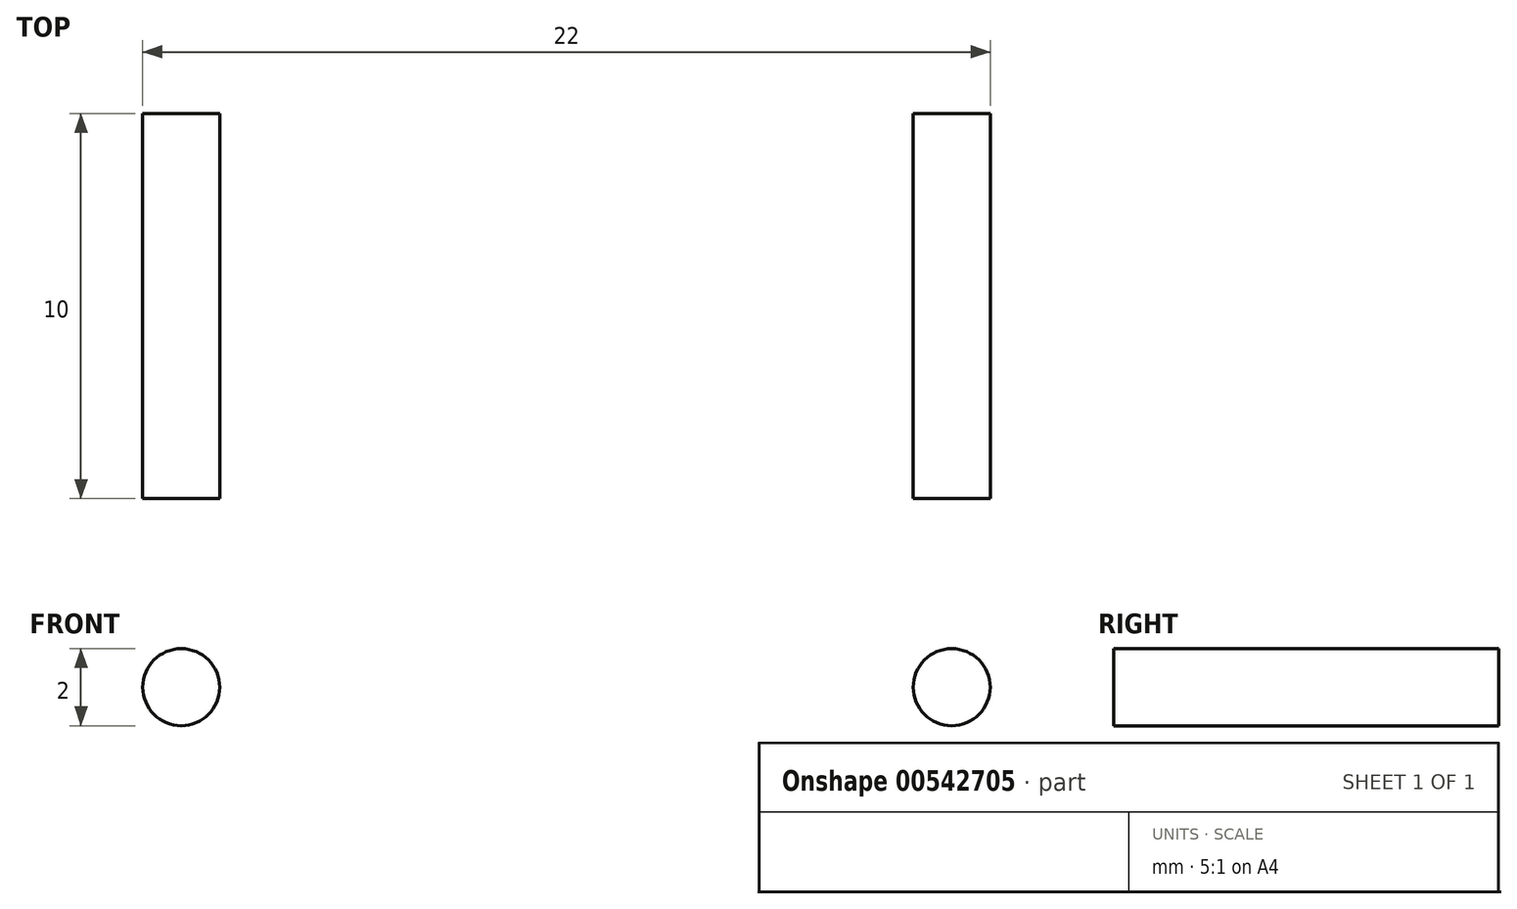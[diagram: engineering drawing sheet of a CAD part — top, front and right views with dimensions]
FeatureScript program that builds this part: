
annotation { "Feature Type Name" : "Feature", "Feature Type Description" : "" }
export const myFeature = defineFeature(function(context is Context, id is Id, definition is map)
    precondition{}
    {
        {
            var Q0;
            Q0=qCreatedBy(makeId("Front.planeOp"),FACE);
            var sketch = newSketch(context, id + "F0", { "sketchPlane" : qUnion([Q0])});
            skArc(sketch, "E0", {"start": v(-9.06, -4.23) * mm, "mid": v(0, 10) * mm, "end": v(9.06, -4.23) * mm});
            skLineSegment(sketch, "E1", {"start": v(-9.06, -4.23) * mm, "end": v(0, 0) * mm, "construction": true});
            skLineSegment(sketch, "E2", {"start": v(9.06, -4.23) * mm, "end": v(0, 0) * mm, "construction": true});
            skLineSegment(sketch, "E3", {"start": v(-9.75, 10.9) * mm, "end": v(-9.75, -4.03) * mm, "construction": true});
            skLineSegment(sketch, "E4", {"start": v(9.75, 10.9) * mm, "end": v(9.75, -4.03) * mm, "construction": true});
            skCircle(sketch, "E5", {"center": v(-10, 0) * mm, "radius": 1 * mm});
            skArc(sketch, "E6.0", {"start": v(-11.33, -5.28) * mm, "mid": v(0, 12.5) * mm, "end": v(11.33, -5.28) * mm});
            skArc(sketch, "E7", {"start": v(-11.33, -5.28) * mm, "mid": v(-9.67, -5.89) * mm, "end": v(-9.06, -4.23) * mm});
            skArc(sketch, "E8", {"start": v(9.06, -4.23) * mm, "mid": v(9.67, -5.89) * mm, "end": v(11.33, -5.28) * mm});
            skCircle(sketch, "E9", {"center": v(10, 0) * mm, "radius": 1 * mm});
            skLineSegment(sketch, "E10", {"start": v(-3.15, 12.1) * mm, "end": v(3.15, 12.1) * mm});
            skPoint(sketch, "E11", {"position": v(0, 12.1) * mm});
            skSolve(sketch);
        }
        {
            var Q0;
            {var subQ0=sQuery(id+"F0.wireOp",EDGE,"E5");var subQ1=sQuery(id+"F0.wireOp",EDGE,"E0");var subQ2=makeQuery(id+"F0.imprint","INTERSECT",VERTEX,{"disambiguationData":[OD(0.0)],"derivedFrom":[subQ1,subQ0]});Q0=makeQuery(id+"F0.imprint","IMPRINT",FACE,{"disambiguationData":[TD([[makeQuery(id+"F0.imprint","IMPRINT",EDGE,{"disambiguationData":[TD([[subQ2,-1.0]])],"derivedFrom":subQ1}),-1.0]])]});}
            var Q1;
            {var subQ0=sQuery(id+"F0.wireOp",EDGE,"E9");var subQ1=sQuery(id+"F0.wireOp",EDGE,"E0");var subQ2=makeQuery(id+"F0.imprint","INTERSECT",VERTEX,{"disambiguationData":[OD(0.0)],"derivedFrom":[subQ1,subQ0]});Q1=makeQuery(id+"F0.imprint","IMPRINT",FACE,{"disambiguationData":[TD([[makeQuery(id+"F0.imprint","IMPRINT",EDGE,{"disambiguationData":[TD([[subQ2,-1.0]])],"derivedFrom":subQ1}),-1.0]])]});}
            var Q2;
            {var subQ0=sQuery(id+"F0.wireOp",EDGE,"E5");var subQ1=sQuery(id+"F0.wireOp",EDGE,"E0");var subQ2=makeQuery(id+"F0.imprint","INTERSECT",VERTEX,{"disambiguationData":[OD(0.0)],"derivedFrom":[subQ1,subQ0]});Q2=makeQuery(id+"F0.imprint","IMPRINT",FACE,{"disambiguationData":[TD([[makeQuery(id+"F0.imprint","IMPRINT",EDGE,{"disambiguationData":[TD([[subQ2,-1.0]])],"derivedFrom":subQ1}),1.0]])]});}
            var Q3;
            {var subQ0=sQuery(id+"F0.wireOp",EDGE,"E9");var subQ1=sQuery(id+"F0.wireOp",EDGE,"E0");var subQ2=makeQuery(id+"F0.imprint","INTERSECT",VERTEX,{"disambiguationData":[OD(0.0)],"derivedFrom":[subQ1,subQ0]});Q3=makeQuery(id+"F0.imprint","IMPRINT",FACE,{"disambiguationData":[TD([[makeQuery(id+"F0.imprint","IMPRINT",EDGE,{"disambiguationData":[TD([[subQ2,-1.0]])],"derivedFrom":subQ1}),1.0]])]});}
            var Q4;
            Q4=makeQuery(id+"F0.imprint","IMPRINT",FACE,{"disambiguationData":[TD([[makeQuery(id+"F0.imprint","IMPRINT",EDGE,{"derivedFrom":sQuery(id+"F0.wireOp",EDGE,"E6.0")}),-1.0]])]});
            extrude(context, id + "F1", {"entities" : qUnion([Q0, Q1, Q2, Q3, Q4]), "depth" : 10 * mm, "offsetDistance" : 25 * mm});
        }
    });
